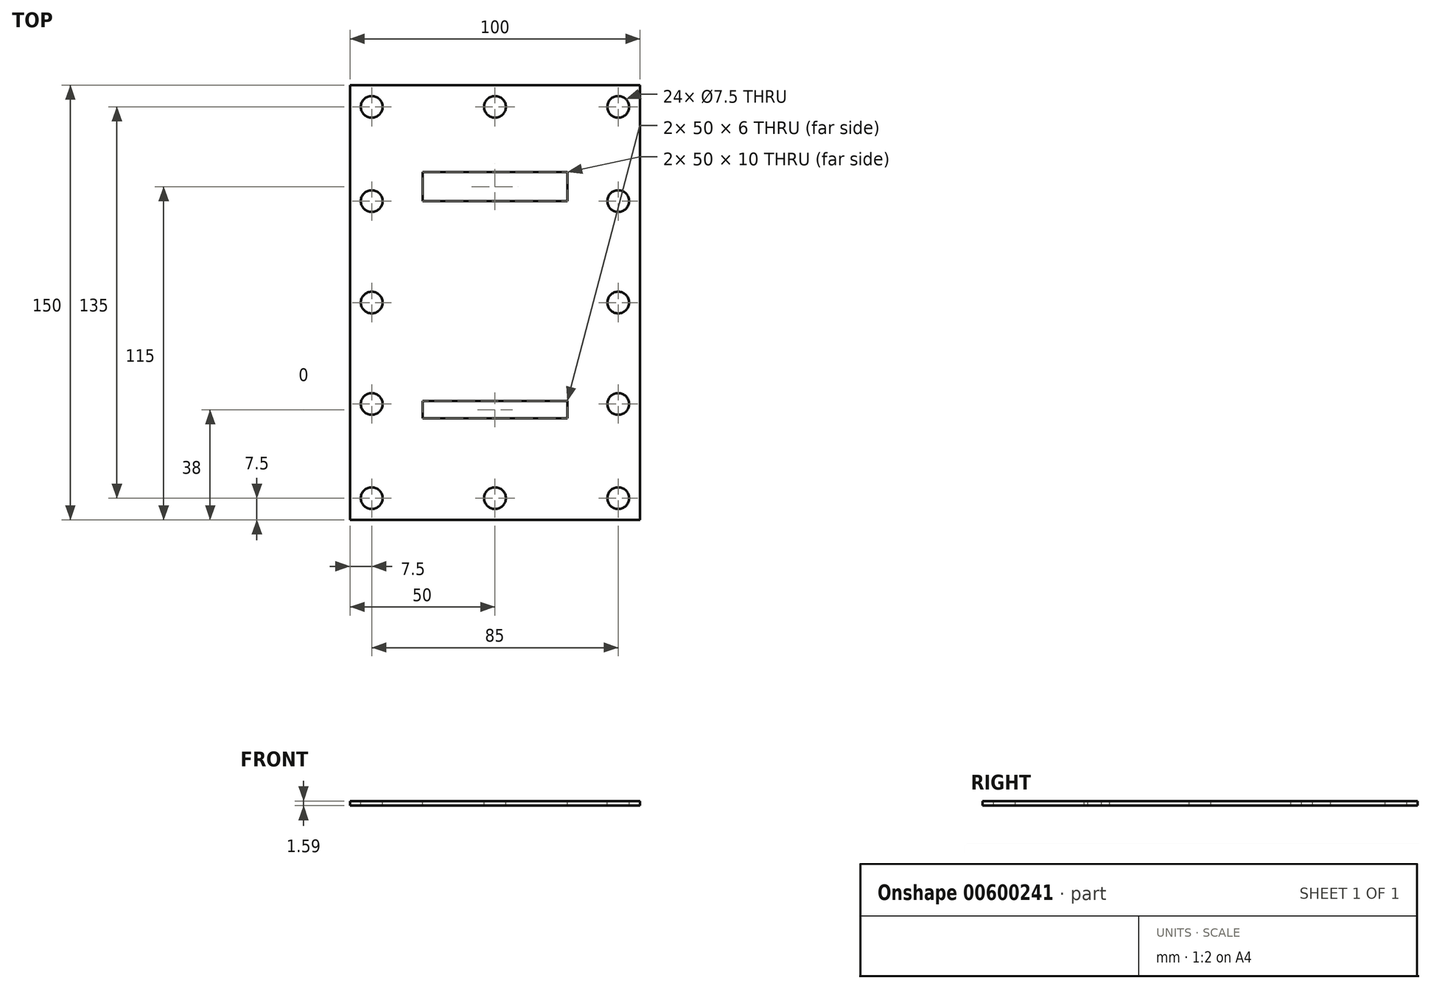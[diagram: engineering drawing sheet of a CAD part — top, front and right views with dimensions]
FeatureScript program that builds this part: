
annotation { "Feature Type Name" : "Feature", "Feature Type Description" : "" }
export const myFeature = defineFeature(function(context is Context, id is Id, definition is map)
    precondition{}
    {
        {
            var Q0;
            Q0=qCreatedBy(makeId("Top.planeOp"),FACE);
            var sketch = newSketch(context, id + "F0", { "sketchPlane" : qUnion([Q0])});
            skLineSegment(sketch, "E0.bottom", {"start": v(50, 75) * mm, "end": v(-50, 75) * mm});
            skLineSegment(sketch, "E0.top", {"start": v(50, -75) * mm, "end": v(-50, -75) * mm});
            skLineSegment(sketch, "E0.left", {"start": v(50, 75) * mm, "end": v(50, -75) * mm});
            skLineSegment(sketch, "E0.right", {"start": v(-50, 75) * mm, "end": v(-50, -75) * mm});
            skPoint(sketch, "E0.middle", {"position": v(0, 0) * mm});
            skSolve(sketch);
        }
        {
            var Q0;
            Q0=qSketchRegion(id+"F0",true);
            var Q1;
            Q1=qSketchRegion(id+"F2",true);
            extrude(context, id + "F1", {"entities" : qUnion([Q0, Q1]), "depth" : 1.59 * mm, "offsetDistance" : 25 * mm});
        }
        {
            var Q0;
            Q0=makeQuery(id+"F1.opExtrude","CAP_FACE",FACE,{"disambiguationData":[OSD([sQuery(id+"F0.wireOp",EDGE,"E0.bottom"),sQuery(id+"F0.wireOp",EDGE,"E0.top"),sQuery(id+"F0.wireOp",EDGE,"E0.left"),sQuery(id+"F0.wireOp",EDGE,"E0.right")])],"isStart":false});
            var sketch = newSketch(context, id + "F2", { "sketchPlane" : qUnion([Q0])});
            skCircle(sketch, "E1", {"center": v(-42.5, 67.5) * mm, "radius": 3.75 * mm});
            skCircle(sketch, "E2", {"center": v(-42.5, 0) * mm, "radius": 3.75 * mm});
            skCircle(sketch, "E3", {"center": v(-42.5, -35) * mm, "radius": 3.75 * mm});
            skCircle(sketch, "E4", {"center": v(-42.5, -67.5) * mm, "radius": 3.75 * mm});
            skCircle(sketch, "E5", {"center": v(0, -67.5) * mm, "radius": 3.75 * mm});
            skCircle(sketch, "E6", {"center": v(-42.5, 35) * mm, "radius": 3.75 * mm});
            skCircle(sketch, "E7", {"center": v(42.5, -67.5) * mm, "radius": 3.75 * mm});
            skCircle(sketch, "E8", {"center": v(42.5, -35) * mm, "radius": 3.75 * mm});
            skCircle(sketch, "E9", {"center": v(42.5, 0) * mm, "radius": 3.75 * mm});
            skCircle(sketch, "E10", {"center": v(42.5, 35) * mm, "radius": 3.75 * mm});
            skCircle(sketch, "E11", {"center": v(42.5, 67.5) * mm, "radius": 3.75 * mm});
            skCircle(sketch, "E12", {"center": v(0, 67.5) * mm, "radius": 3.75 * mm});
            skSolve(sketch);
        }
        {
            var Q0;
            Q0=qSketchRegion(id+"F2",true);
            extrude(context, id + "F3", {"entities" : qUnion([Q0]), "operationType" : NewBodyOperationType.REMOVE, "oppositeDirection" : true, "depth" : 25 * mm, "offsetDistance" : 25 * mm});
        }
        {
            var Q0;
            Q0=makeQuery(id+"F1.opExtrude","CAP_FACE",FACE,{"disambiguationData":[OSD([sQuery(id+"F0.wireOp",EDGE,"E0.bottom"),sQuery(id+"F0.wireOp",EDGE,"E0.top"),sQuery(id+"F0.wireOp",EDGE,"E0.left"),sQuery(id+"F0.wireOp",EDGE,"E0.right")])],"isStart":false});
            var sketch = newSketch(context, id + "F4", { "sketchPlane" : qUnion([Q0])});
            skLineSegment(sketch, "E13.bottom", {"start": v(25, -40) * mm, "end": v(-25, -40) * mm});
            skLineSegment(sketch, "E13.top", {"start": v(25, -34) * mm, "end": v(-25, -34) * mm});
            skLineSegment(sketch, "E13.left", {"start": v(25, -40) * mm, "end": v(25, -34) * mm});
            skLineSegment(sketch, "E13.right", {"start": v(-25, -40) * mm, "end": v(-25, -34) * mm});
            skPoint(sketch, "E13.middle", {"position": v(0, -37) * mm});
            skSolve(sketch);
        }
        {
            var Q0;
            Q0 = qSketchRegion(id + "F4", true);
            extrude(context, id + "F5", {"entities" : qUnion([Q0]), "operationType" : NewBodyOperationType.REMOVE, "oppositeDirection" : true, "depth" : 25 * mm, "offsetDistance" : 25 * mm});
        }
        {
            var Q0;
            Q0=makeQuery(id+"F1.opExtrude","CAP_FACE",FACE,{"disambiguationData":[OSD([sQuery(id+"F0.wireOp",EDGE,"E0.bottom"),sQuery(id+"F0.wireOp",EDGE,"E0.top"),sQuery(id+"F0.wireOp",EDGE,"E0.left"),sQuery(id+"F0.wireOp",EDGE,"E0.right")])],"isStart":false});
            var sketch = newSketch(context, id + "F6", { "sketchPlane" : qUnion([Q0])});
            skLineSegment(sketch, "E14.bottom", {"start": v(25, 35) * mm, "end": v(-25, 35) * mm});
            skLineSegment(sketch, "E14.top", {"start": v(25, 45) * mm, "end": v(-25, 45) * mm});
            skLineSegment(sketch, "E14.left", {"start": v(25, 35) * mm, "end": v(25, 45) * mm});
            skLineSegment(sketch, "E14.right", {"start": v(-25, 35) * mm, "end": v(-25, 45) * mm});
            skPoint(sketch, "E14.middle", {"position": v(0, 40) * mm});
            skSolve(sketch);
        }
        {
            var Q0;
            Q0 = qSketchRegion(id + "F6", true);
            extrude(context, id + "F7", {"entities" : qUnion([Q0]), "operationType" : NewBodyOperationType.REMOVE, "oppositeDirection" : true, "depth" : 25 * mm, "offsetDistance" : 25 * mm});
        }
    });
